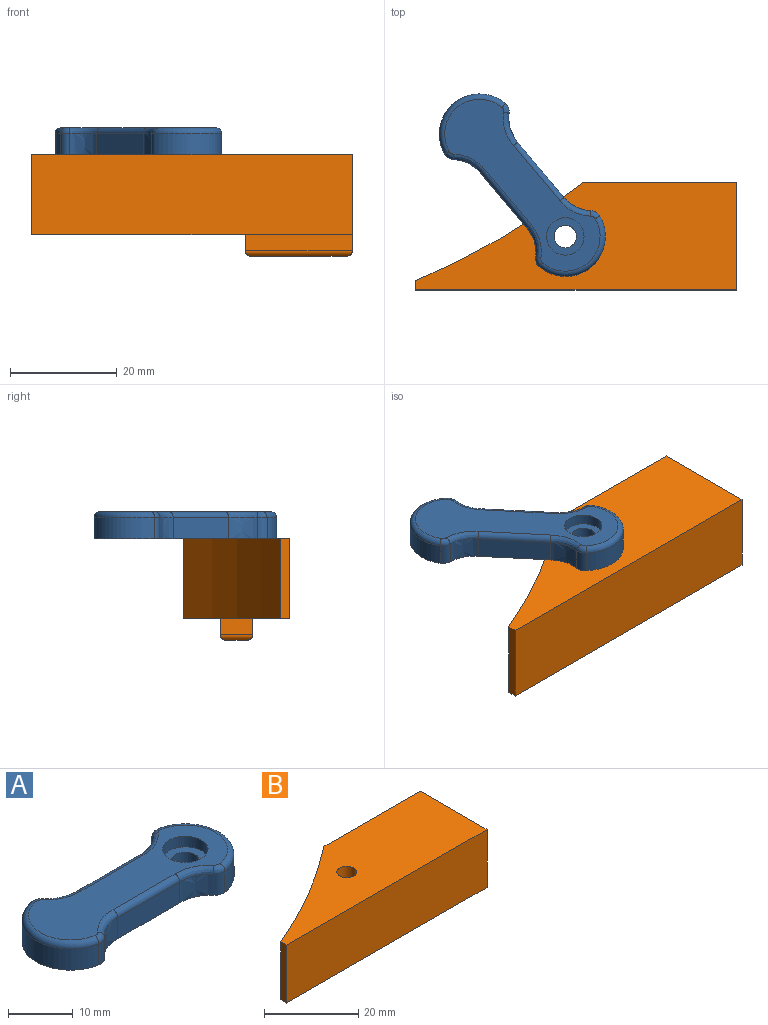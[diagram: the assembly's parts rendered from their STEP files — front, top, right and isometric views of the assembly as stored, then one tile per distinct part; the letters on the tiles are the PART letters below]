
ASSEMBLY  parts=2 mates=1
PART A: 29 faces, bbox 41.2x16x5.5 mm
  f0: plane 38x12.85mm, normal (0,0,1), area 285mm2, adj f6,f17,f18,f19,f20,f21,f22,f23
  f1: cylinder r=7.5mm len=14.79mm, axis (0,0,-1), area 84.3mm2, adj f3,f14,f15,f28
  f2: cylinder r=7.5mm len=14.79mm, axis (0,0,-1), area 84.3mm2, adj f3,f13,f16,f17
  f3: plane 40x14.85mm, normal (0,0,-1), area 407mm2, adj f1,f2,f4,f7,f8,f9,f10,f11
  f4: cylinder r=2.1mm len=4.2mm, axis (0,0,1), area 39.6mm2, adj f3,f5
  f5: plane 7x7mm, normal (0,0,1), area 24.6mm2, adj f4,f6
  f6: cylinder r=3.5mm len=7mm, axis (0,0,1), area 44mm2, adj f0,f5
  f7: plane 13.51x4mm, normal (0,-1,0), area 54mm2, adj f3,f9,f10,f22
  f8: plane 13.51x4mm, normal (0,1,0), area 54mm2, adj f3,f11,f12,f23
  f9: bspline ~5.74x5.5mm, area 23.2mm2, adj f3,f7,f16,f20
  f10: bspline ~5.74x5.5mm, area 23.2mm2, adj f3,f7,f14,f24
  f11: bspline ~5.74x5.5mm, area 23.2mm2, adj f3,f8,f13,f21
  f12: bspline ~5.74x5.5mm, area 23.2mm2, adj f3,f8,f15,f25
  f13: cylinder r=2mm len=4mm, axis (0,0,-1), area 8.1mm2, adj f2,f3,f11,f19
  f14: cylinder r=2mm len=4mm, axis (0,0,-1), area 8.1mm2, adj f1,f3,f10,f26
  f15: cylinder r=2mm len=4mm, axis (0,0,-1), area 8.1mm2, adj f1,f3,f12,f27
  f16: cylinder r=2mm len=4mm, axis (0,0,-1), area 8.1mm2, adj f2,f3,f9,f18
  f17: torus R=6.5mm, axis (0,0,1), area 31.5mm2, adj f0,f2,f18,f19
  f18: torus R=1mm, axis (0,0,1), area 2.6mm2, adj f0,f16,f17,f20
  f19: torus R=1mm, axis (0,0,1), area 2.6mm2, adj f0,f13,f17,f21
  f20: bspline ~7.92x3.55mm, area 9.6mm2, adj f0,f9,f18,f22
  f21: bspline ~7.92x3.55mm, area 9.6mm2, adj f0,f11,f19,f23
  f22: cylinder r=1mm len=13.51mm, axis (-1,0,0), area 21.2mm2, adj f0,f7,f20,f24
  f23: cylinder r=1mm len=13.51mm, axis (1,0,0), area 21.2mm2, adj f0,f8,f21,f25
  f24: bspline ~7.92x3.55mm, area 9.6mm2, adj f0,f10,f22,f26
  f25: bspline ~7.92x3.55mm, area 9.6mm2, adj f0,f12,f23,f27
  f26: torus R=1mm, axis (0,0,1), area 2.6mm2, adj f0,f14,f24,f28
  f27: torus R=1mm, axis (0,0,1), area 2.6mm2, adj f0,f15,f25,f28
  f28: torus R=6.5mm, axis (0,0,1), area 31.5mm2, adj f0,f1,f26,f27
PART B: 16 faces, bbox 60x20x19 mm
  f0: plane 60x20mm, normal (0,0,-1), area 752.5mm2, adj f1,f2,f4,f5,f6,f8,f9,f14
  f1: plane 28.84x15mm, normal (0,1,0), area 432.5mm2, adj f0,f3,f5,f14
  f2: plane 15x1.72mm, normal (-1,0,0), area 25.8mm2, adj f0,f3,f4,f14
  f3: plane 60x20mm, normal (0,0,1), area 872.5mm2, adj f1,f2,f4,f5,f14,f15
  f4: plane 60x15mm, normal (0,-1,0), area 900mm2, adj f0,f2,f3,f5
  f5: plane 20x18mm, normal (1,0,0), area 318mm2, adj f0,f1,f3,f4,f6,f8,f12
  f6: plane 20x3mm, normal (0,-1,0), area 60mm2, adj f0,f5,f9,f13
  f7: plane 18x4mm, normal (0,0,-1), area 72mm2, adj f10,f11,f12,f13
  f8: plane 20x3mm, normal (0,1,0), area 60mm2, adj f0,f5,f9,f10
  f9: plane 6x3mm, normal (-1,0,0), area 18mm2, adj f0,f6,f8,f11
  f10: cylinder r=1mm len=20mm, axis (-1,0,0), area 30.3mm2, adj f7,f8,f11,f12
  f11: cylinder r=1mm len=6mm, axis (0,-1,0), area 8.3mm2, adj f7,f9,f10,f13
  f12: cylinder r=1mm len=6mm, axis (0,1,0), area 8.3mm2, adj f5,f7,f10,f13
  f13: cylinder r=1mm len=20mm, axis (1,0,0), area 30.3mm2, adj f6,f7,f11,f12
  f14: cylinder r=137mm len=31.16mm, axis (0,0,-1), area 543.5mm2, adj f0,f1,f2,f3
  f15: cylinder r=2.1mm len=15mm, axis (0,0,1), area 197.9mm2, adj f0,f3
PLACE A rot(axis=(0,0,-1),50deg) t=(-11.43,-24.51,0)mm
PLACE B at identity
MATE revolute A.f1 <-> B.f15  axis (0,0,-1) through (-32,0,15)mm
